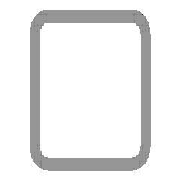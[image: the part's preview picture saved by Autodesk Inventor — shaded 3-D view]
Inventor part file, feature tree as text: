
AUTODESK INVENTOR PART (.ipt)
format: ipt  version: 2025 (Build 290162010, 162A)  size: 136,704 bytes
history: native  units: mm (DEFAULTED — no unit token found)
features: other x4, sketch x1, plane x1
ambient origin geometry x8: Origin, YZ Plane, XZ Plane, XY Plane, X Axis, Y Axis, Z Axis, Center Point
bodies: Solid1 (feature_tree), Body (feature_tree)
feature tree (6):
  parser-record x1  (decoder bookkeeping rows leaked as tree rows — omitted from the tree; the rows remain in map.json)
  other  "Driven Length"
  other  "Start Plane"
  other  "End Plane"
  sketch  "Sketch3"  dims[d3=1420.0mm d4=0.0mm d7=4.0mm d9=40.0mm d11=40.0mm d12=2.0mm d13=40.0mm d14=1460.0mm d15=20.0mm d16=20.0mm d17=90.0deg d18=1420.0mm]
  plane  "Work Plane3"
